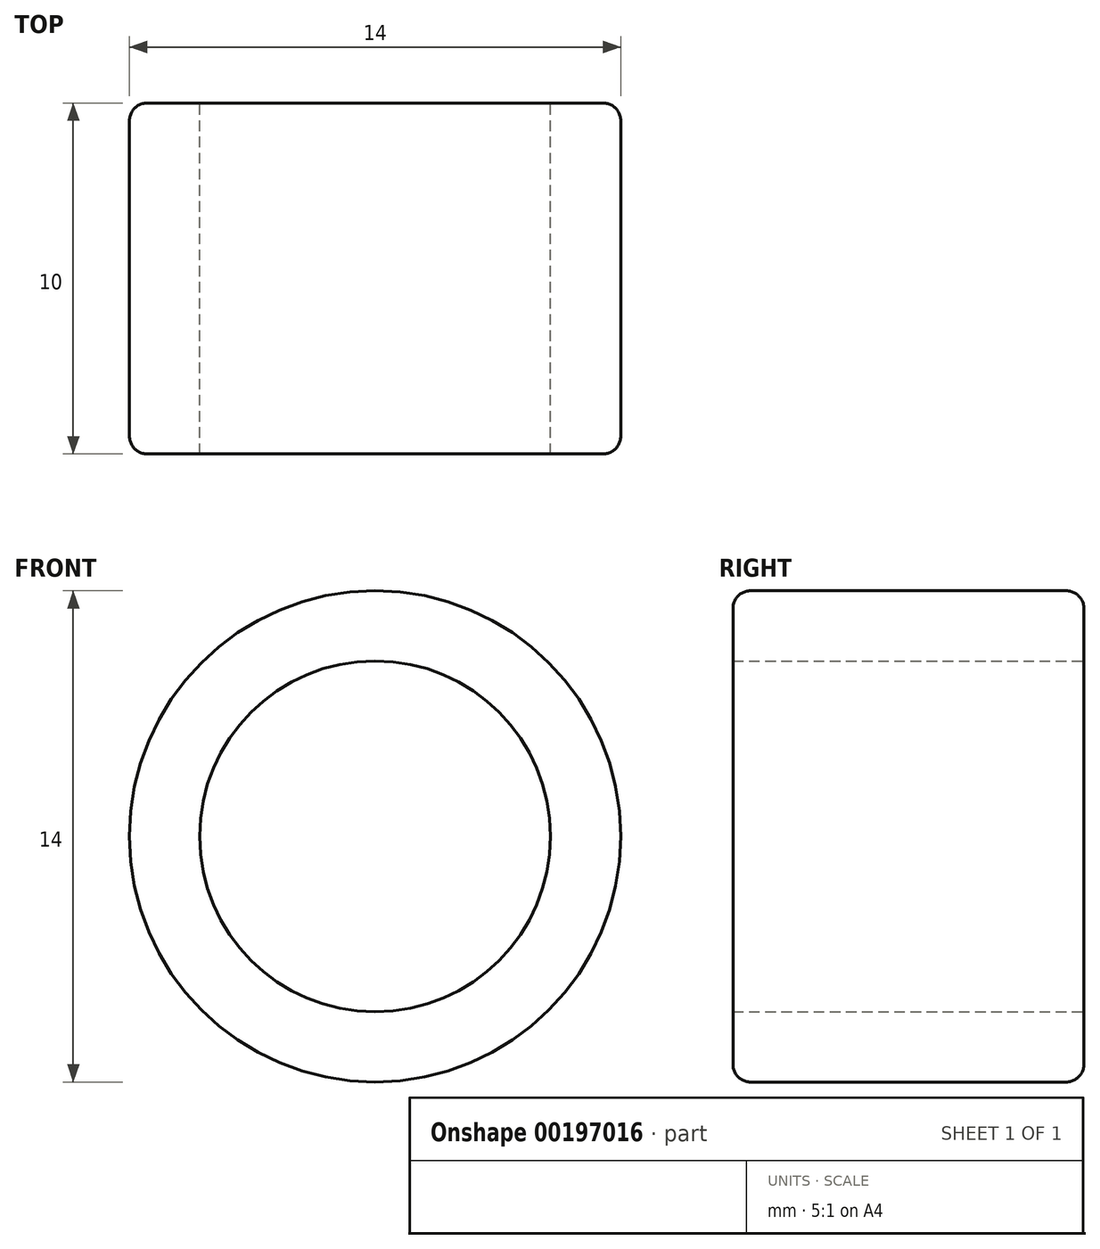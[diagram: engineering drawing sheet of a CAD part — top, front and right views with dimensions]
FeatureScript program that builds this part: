
annotation { "Feature Type Name" : "Feature", "Feature Type Description" : "" }
export const myFeature = defineFeature(function(context is Context, id is Id, definition is map)
    precondition{}
    {
        {
            var Q0;
            Q0=qCreatedBy(makeId("Front.planeOp"),FACE);
            var sketch = newSketch(context, id + "F0", { "sketchPlane" : qUnion([Q0])});
            skCircle(sketch, "E0", {"center": v(0, 0) * mm, "radius": 7 * mm});
            skCircle(sketch, "E1", {"center": v(0, 0) * mm, "radius": 5 * mm});
            skSolve(sketch);
        }
        {
            var Q0;
            Q0 = qSketchRegion(id + "F0", true);
            extrude(context, id + "F1", {"entities" : qUnion([Q0]), "endBound" : BoundingType.SYMMETRIC, "depth" : 10 * mm});
        }
        {
            var Q0;
            Q0=makeQuery(id+"F1.opExtrude","SWEPT_FACE",FACE,{"disambiguationData":[OSD([sQuery(id+"F0.wireOp",EDGE,"E0")])]});
            fillet(context, id + "F2", {"entities" : qUnion([Q0]), "radius" : .5 * mm, "tangentPropagation" : true, "allowEdgeOverflow" : false});
        }
    });
